# Revit family: Volleyball-Adjustable_Plataform-Clamp_On-IPIbyBison-VB73A
name_source: partatom
category: Specialty Equipment
units: mm (PartAtom-declared; Revit-internal decimal feet)

## family parameters
Always vertical = Yes
Cut with Voids When Loaded = No
Maintain Annotation Orientation = No
OmniClass Number = 23.40.50.34.14
OmniClass Title = Gymnasium Equipment
Part Type = Normal
Room Calculation Point = No
Round Connector Dimension = Use Diameter
Shared = No
Work Plane-Based = No

## types (1)
- VB73A
    CAD Details = https://www.arcat.com
    Default Elevation = 0' - 0"
    Description = Volleyball Portable Equipment Adjustable
    Frame Material = Powder Coat - Gray
    Keynote = 11 66 00
    Length = 2' - 11"
    Manufacturer = IPI by Bison
    Model = VB73A
    Padding = Padding - Specify Color
    Product Page URL = https://www.arcat.com
    Specification = https://www.arcat.com
    URL = https://ipibybison.com
    Width = 1' - 11"

## geometry (parser evidence)
native form markers: Sweep x3
no freeform markers — native parametric forms only
